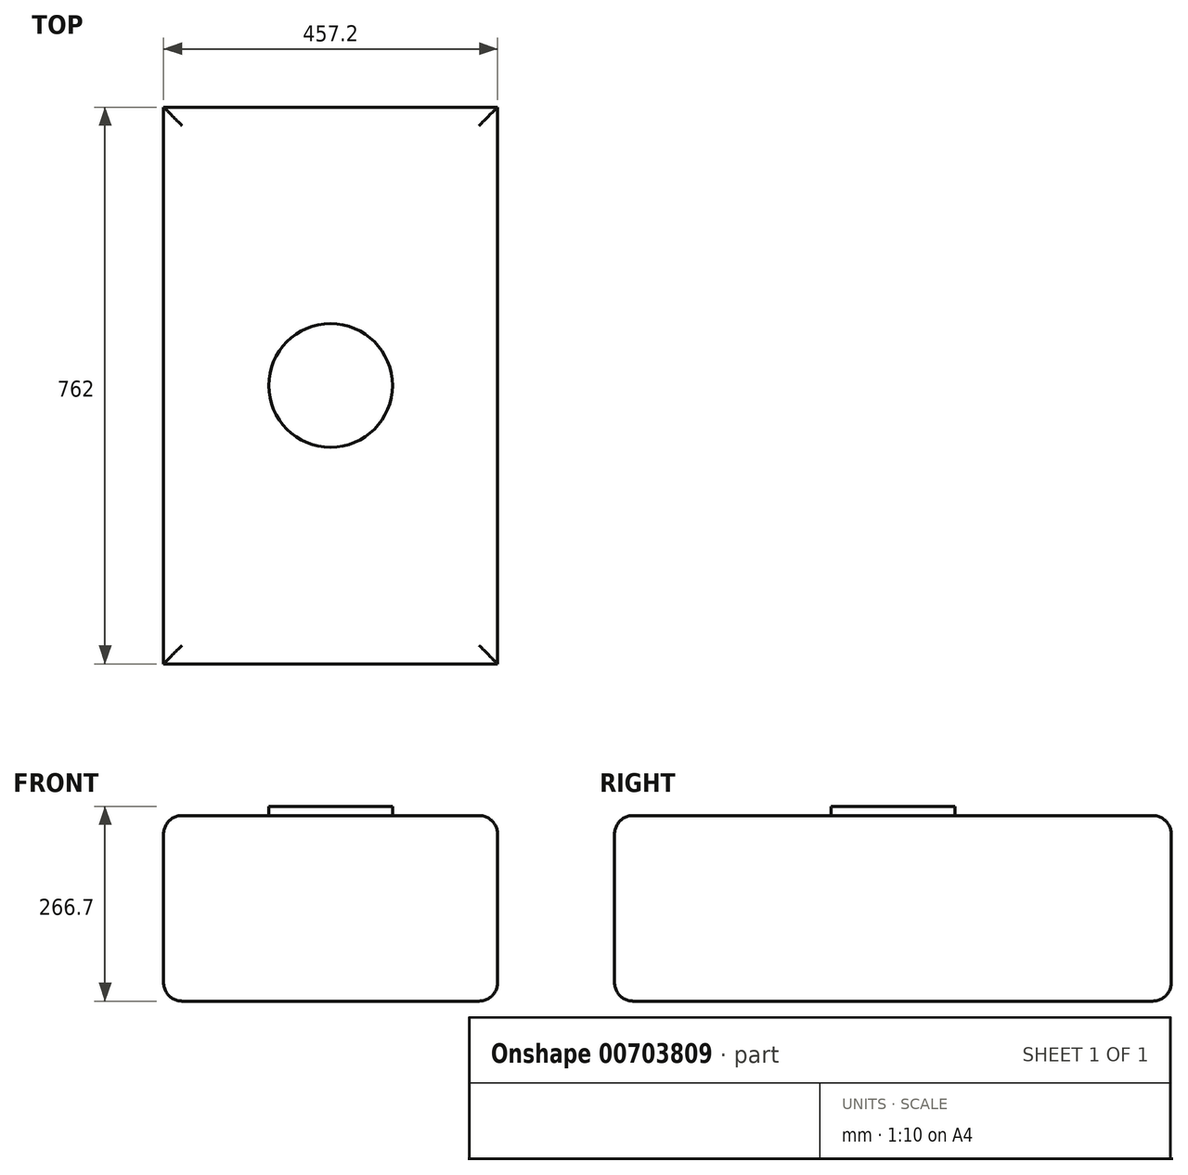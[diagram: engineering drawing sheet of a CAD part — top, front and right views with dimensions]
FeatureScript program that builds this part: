
annotation { "Feature Type Name" : "Feature", "Feature Type Description" : "" }
export const myFeature = defineFeature(function(context is Context, id is Id, definition is map)
    precondition{}
    {
        {
            var Q0;
            Q0=qCreatedBy(makeId("Top.planeOp"),FACE);
            var sketch = newSketch(context, id + "F0", { "sketchPlane" : qUnion([Q0])});
            skLineSegment(sketch, "E0.bottom", {"start": v(-228.6, -381) * mm, "end": v(228.6, -381) * mm});
            skLineSegment(sketch, "E0.top", {"start": v(-228.6, 381) * mm, "end": v(228.6, 381) * mm});
            skLineSegment(sketch, "E0.left", {"start": v(-228.6, -381) * mm, "end": v(-228.6, 381) * mm});
            skLineSegment(sketch, "E0.right", {"start": v(228.6, -381) * mm, "end": v(228.6, 381) * mm});
            skPoint(sketch, "E0.middle", {"position": v(0, 0) * mm});
            skSolve(sketch);
        }
        {
            var Q0;
            Q0=makeQuery(id+"F0.imprint","IMPRINT",FACE,{"disambiguationData":[TD([[makeQuery(id+"F0.imprint","IMPRINT",EDGE,{"derivedFrom":sQuery(id+"F0.wireOp",EDGE,"E0.bottom")}),1.0]])]});
            extrude(context, id + "F1", {"entities" : qUnion([Q0]), "depth" : 254 * mm, "offsetDistance" : 25.4 * mm});
        }
        {
            var Q0;
            Q0=makeQuery(id+"F1.opExtrude","CAP_EDGE",EDGE,{"disambiguationData":[OSD([sQuery(id+"F0.wireOp",EDGE,"E0.top")])],"isStart":false});
            var Q1;
            Q1=makeQuery(id+"F1.opExtrude","CAP_EDGE",EDGE,{"disambiguationData":[OSD([sQuery(id+"F0.wireOp",EDGE,"E0.right")])],"isStart":false});
            var Q2;
            Q2=makeQuery(id+"F1.opExtrude","CAP_EDGE",EDGE,{"disambiguationData":[OSD([sQuery(id+"F0.wireOp",EDGE,"E0.bottom")])],"isStart":false});
            var Q3;
            Q3=makeQuery(id+"F1.opExtrude","CAP_EDGE",EDGE,{"disambiguationData":[OSD([sQuery(id+"F0.wireOp",EDGE,"E0.left")])],"isStart":false});
            var Q4;
            Q4=makeQuery(id+"F1.opExtrude","CAP_EDGE",EDGE,{"disambiguationData":[OSD([sQuery(id+"F0.wireOp",EDGE,"E0.right")])],"isStart":true});
            var Q5;
            Q5=makeQuery(id+"F1.opExtrude","CAP_FACE",FACE,{"disambiguationData":[OSD([sQuery(id+"F0.wireOp",EDGE,"E0.bottom"),sQuery(id+"F0.wireOp",EDGE,"E0.top"),sQuery(id+"F0.wireOp",EDGE,"E0.left"),sQuery(id+"F0.wireOp",EDGE,"E0.right")])],"isStart":true});
            fillet(context, id + "F2", {"entities" : qUnion([Q0, Q1, Q2, Q3, Q4, Q5]), "radius" : 25.4 * mm, "tangentPropagation" : true, "allowEdgeOverflow" : false});
        }
        {
            var Q0;
            Q0=makeQuery(id+"F1.opExtrude","CAP_FACE",FACE,{"disambiguationData":[OSD([sQuery(id+"F0.wireOp",EDGE,"E0.bottom"),sQuery(id+"F0.wireOp",EDGE,"E0.top"),sQuery(id+"F0.wireOp",EDGE,"E0.left"),sQuery(id+"F0.wireOp",EDGE,"E0.right")])],"isStart":false});
            var sketch = newSketch(context, id + "F3", { "sketchPlane" : qUnion([Q0])});
            skCircle(sketch, "E1", {"center": v(0, 0) * mm, "radius": 84.66 * mm});
            skSolve(sketch);
        }
        {
            var Q0;
            Q0=makeQuery(id+"F3.imprint","IMPRINT",FACE,{"disambiguationData":[TD([[makeQuery(id+"F3.imprint","IMPRINT",EDGE,{"derivedFrom":sQuery(id+"F3.wireOp",EDGE,"E1")}),1.0]])]});
            extrude(context, id + "F4", {"entities" : qUnion([Q0]), "operationType" : NewBodyOperationType.ADD, "depth" : 12.7 * mm, "offsetDistance" : 25.4 * mm});
        }
    });
